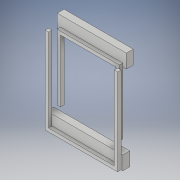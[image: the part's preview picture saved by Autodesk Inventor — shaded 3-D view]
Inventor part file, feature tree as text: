
AUTODESK INVENTOR PART (.ipt)
format: ipt  version: 2017 (Build 210142000, 142)  size: 167,424 bytes
history: native  units: in
note: dims shown in document units (in); Inventor stores cm internally (conversion verified against a paired STEP export)
features: sketch x9, extrude x6, thicken_offset x2
ambient origin geometry x8: Origin, YZ Plane, XZ Plane, XY Plane, X Axis, Y Axis, Z Axis, Center Point
bodies: Solid1 (feature_tree)
feature tree (17):
  extrude  "Extrusion1"  Depth=2.0in
  extrude  "Extrusion2"  Depth=10.0in
  extrude  "Extrusion3"  Depth=2.0in
  thicken_offset  "Thicken1"
  thicken_offset  "Thicken2"
  sketch  "Sketch4"  dims[d7=1.0in d8=0.0in d9=0.5in]
  sketch  "Sketch5"  dims[d10=0.5in d11=0.0in d12=0.5in]
  sketch  "Sketch6"  dims[d13=0.5in d14=0.5in]
  extrude  "Extrusion4"  Depth=0.5in
  extrude  "Extrusion5"  Depth=0.5in
  extrude  "Extrusion6"  Depth=0.5in
  sketch  "Sketch1"  dims[d0=10.0in d1=2.0in]
  sketch  "Sketch2"  dims[d2=1.0in d3=0.0in d4=10.0in]
  sketch  "Sketch3"  dims[d5=0.0in d6=2.0in]
  sketch  "Sketch7"  dims[d15=0.5in]
  sketch  "Sketch8"  dims[d16=0.5in]
  sketch  "Sketch9"  dims[d17=0.5in d18=0.0in d19=0.5in d20=0.5in d21=12.0in d22=0.0in d23=0.5in d24=0.5in d25=0.5in d26=9.0in d27=0.0in]
